# Revit family: NLRS_57_AIR_UN_steel wheather wall louvre bmu intake LT_sacs
name_source: partatom
category: Air Terminals
revit_build: Autodesk Revit 2018 (Build: 20190510_1515(x64)
units: mm (PartAtom-declared; Revit-internal decimal feet)

## family parameters
Always vertical = No
Cut with Voids When Loaded = Yes
OmniClass Number = 23.75.70.21.27.11
OmniClass Title = Diffusers, Registers, and Grilles
Part Type = Normal
Room Calculation Point = Yes
Round Connector Dimension = Use Diameter
Shared = No
Work Plane-Based = No

## types (6) — shared parameters
Assembly Code = 57.0
Description = Solid Air weather louvre BMU (air intake)
FireRating = 0
IfcDescription = Solid Air weather louvre BMU (air intake)
IfcExportAs = IfcAirTerminal
IfcExportType = LOUVRE
IsExternal = No
LoadBearing = No
LookupTable = BMU
Manufacturer = Solid Air Climate Systems
Max Flow = 0.0 m³/h
Min Flow = 0.0 m³/h
Model = Weather louvre
NLRS_C_content_datum_uitgifte = 12-04-2021
NLRS_C_content_provider = Solid Air Climate Solutions
NLRS_C_content_versie = 3.18.01
NLRS_C_niveau ontwikkeling = LOD 400
SACS_Material_Frame = Hot dip galvanised steel
SACS_Show_Symbol = No
URL = https://solid-air.nl

## per-type parameters (varying)
| type | SACS_Base_Index | SACS_Factor_NDF1 | SACS_Factor_NDF2 | SACS_Factor_NDF3 | SACS_Factor_NDF4 | SACS_Factor_NDF5 | SACS_Factor_NDF6 | SACS_Frame_1 | SACS_Frame_2 | SACS_Material_Wire_mesh |
| BMUFQK | 1 | -2.4e-05 | 2e-06 | 0.004564 | -0.342326 | -0.159752 | 12.437854 | Yes | No | 10x10mm hot dip galvanised |
| BMUFSK | 2 | -36075.036108 | 71117.678239 | 0.003423 | -0.256715 | -0.119817 | 9.302894 | Yes | No | 2x2 stainless steel |
| BMUFQQ | 3 | -2.4e-05 | 2e-06 | 0.004564 | -0.342326 | -0.159752 | 12.437854 | No | Yes | 2x2 stainless steel |
| BMUDQQ | 5 | -2.4e-05 | 2e-06 | 0.004564 | -0.342326 | -0.159752 | 12.437854 | No | No | 2x2 stainless steel |
| BMUDSQ | 6 | -36075.036108 | 71117.678239 | 0.003423 | -0.256715 | -0.119817 | 9.302894 | No | No | 2x2 stainless steel |
| BMUFSQ | 4 | -36075.036108 | 711173678239 | 0.003423 | -0.256715 | -0.119817 | 9.302894 | No | Yes | 2x2 stainless steel |

## geometry (parser evidence)
native form markers: Sweep x10
no freeform markers — native parametric forms only
